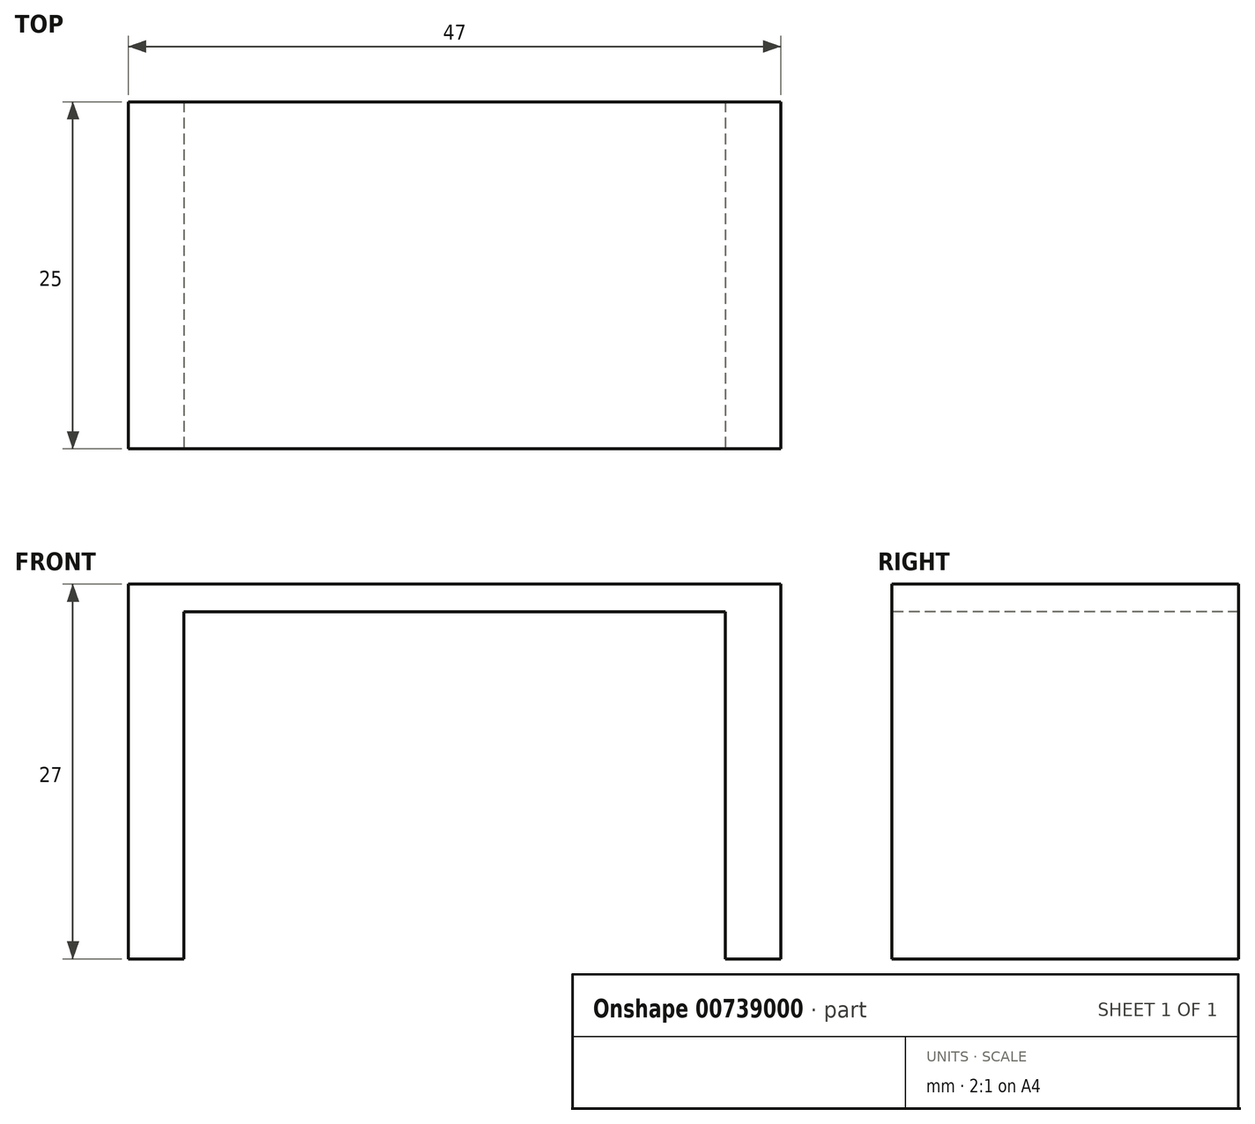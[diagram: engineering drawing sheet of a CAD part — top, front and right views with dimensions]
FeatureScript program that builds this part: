
annotation { "Feature Type Name" : "Feature", "Feature Type Description" : "" }
export const myFeature = defineFeature(function(context is Context, id is Id, definition is map)
    precondition{}
    {
        {
            var Q0;
            Q0=qCreatedBy(makeId("Top.planeOp"),FACE);
            var sketch = newSketch(context, id + "F0", { "sketchPlane" : qUnion([Q0])});
            skLineSegment(sketch, "E0.bottom", {"start": v(-19.5, 12.5) * mm, "end": v(-23.5, 12.5) * mm});
            skLineSegment(sketch, "E0.top", {"start": v(-19.5, -12.5) * mm, "end": v(-23.5, -12.5) * mm});
            skLineSegment(sketch, "E0.left", {"start": v(-19.5, 12.5) * mm, "end": v(-19.5, -12.5) * mm});
            skLineSegment(sketch, "E0.right", {"start": v(-23.5, 12.5) * mm, "end": v(-23.5, -12.5) * mm});
            skPoint(sketch, "E0.middle", {"position": v(-21.5, 0) * mm});
            skLineSegment(sketch, "E1.bottom", {"start": v(23.5, 12.5) * mm, "end": v(19.5, 12.5) * mm});
            skLineSegment(sketch, "E1.top", {"start": v(23.5, -12.5) * mm, "end": v(19.5, -12.5) * mm});
            skLineSegment(sketch, "E1.left", {"start": v(23.5, 12.5) * mm, "end": v(23.5, -12.5) * mm});
            skLineSegment(sketch, "E1.right", {"start": v(19.5, 12.5) * mm, "end": v(19.5, -12.5) * mm});
            skPoint(sketch, "E1.middle", {"position": v(21.5, 0) * mm});
            skLineSegment(sketch, "E2", {"start": v(-21.5, 0) * mm, "end": v(0, 0) * mm, "construction": true});
            skLineSegment(sketch, "E3", {"start": v(0, 0) * mm, "end": v(21.5, 0) * mm, "construction": true});
            skSolve(sketch);
        }
        {
            var Q0;
            Q0 = qSketchRegion(id + "F0", true);
            extrude(context, id + "F1", {"entities" : qUnion([Q0]), "depth" : 25 * mm, "offsetDistance" : 25 * mm});
        }
        {
            var Q0;
            Q0=makeQuery(id+"F1.opExtrude","CAP_FACE",FACE,{"disambiguationData":[OSD([sQuery(id+"F0.wireOp",EDGE,"E1.bottom"),sQuery(id+"F0.wireOp",EDGE,"E1.top"),sQuery(id+"F0.wireOp",EDGE,"E1.left"),sQuery(id+"F0.wireOp",EDGE,"E1.right")])],"isStart":false});
            var sketch = newSketch(context, id + "F2", { "sketchPlane" : qUnion([Q0])});
            skLineSegment(sketch, "E4.bottom", {"start": v(-23.5, 12.5) * mm, "end": v(23.5, 12.5) * mm});
            skLineSegment(sketch, "E4.top", {"start": v(-23.5, -12.5) * mm, "end": v(23.5, -12.5) * mm});
            skLineSegment(sketch, "E4.left", {"start": v(-23.5, 12.5) * mm, "end": v(-23.5, -12.5) * mm});
            skLineSegment(sketch, "E4.right", {"start": v(23.5, 12.5) * mm, "end": v(23.5, -12.5) * mm});
            skSolve(sketch);
        }
        {
            var Q0;
            Q0 = qSketchRegion(id + "F2", true);
            extrude(context, id + "F3", {"entities" : qUnion([Q0]), "operationType" : NewBodyOperationType.ADD, "depth" : 2 * mm, "offsetDistance" : 25 * mm});
        }
    });
